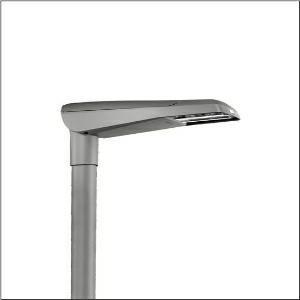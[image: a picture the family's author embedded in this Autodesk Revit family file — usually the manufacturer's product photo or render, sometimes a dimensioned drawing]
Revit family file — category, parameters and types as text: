
# Revit family: streetlight_sl_11_iq_micro___st1_2a_5xc1a61f08ce_98e9
name_source: partatom
category: Lighting Fixtures
units: mm (PartAtom-declared; Revit-internal decimal feet)

## family parameters
Cut with Voids When Loaded = No
Host = Face
Light Source = No
Part Type = Normal
Room Calculation Point = No
Round Connector Dimension = Use Diameter
Shared = No

## types (1)
- --- (1 x LED, 1690 lm, 12.6 W, 2700K)
    Apparent Load = 13 VA
    CIE Flux Codes = 33 71 96 100 100
    Color Rendering = 70
    Color Temperature = 2700K
    Default Elevation = 1800 mm
    Description = Streetlight SL 11 iQ micro, mast luminaire, primary light control with 3 zone facetted reflector, of plastic, silver coated, highly specular, primary optical cover: cover, of PMMA, transparent, light distribution: ST1.2a, light emission: direct distribution, primary light characteristic: asymmetric, installation type: side-entry, post-top, lamps: LED, High Power LED, rated values: 1.690lm | 12,6W | 134,1lm/W (begin service life); end service life: 1.690lm | 12,9W; at 50% lumin. flux: 845lm | 6,8W | 124,3lm/W, colour temperature: 2700K, colour rendering: CRI > 70, light colour: 727, light setting 1 begin service life: 100% | 1.690lm | 12,6W | 134,1lm/W | 2.700K, light setting 1 end service life: 12,9W, further light settings possible, control: optimised constant luminous flux control (CLO 2.0), Desk-Remote (wireless, voltage-free reading and setting of iQ features in the workshop via application-optimized NFC function/RFID function), Light-Fading, Smart-Wire, Night-Set, Lumen-Switch, Temp-Guard, Auto-Match, Street-Remote, with cable H07RN-F 3x 1.5mm², mains connection: 230..240V, AC, 50/60Hz, connection cable pre-assembled, cable length: 5,5m, luminaire housing, of diecast aluminium, powder-coated, SITECO metallic grey (DB 702S), please order mast flange separately, inclination adjustable without tools: 0°, 5°, 10°, 15° (post-top) | 0°, -5°, -10°, -15° (side-entry), sealing non-destructively replaceable, multi-level sealing system, length: 600mm, width: 174mm, height: 116mm, mast flange for spigot size: 42mm (side-entry): 5XC10008XM4, 60/48mm (side-entry/post-top): 5XC10108XM2, 76/60mm (side-entry/post-top): 5XC10108XM1, equipment: standard, protection rating (complete): IP66, insulation class (complete): insulation class II (safety insulation), certification: CE, ENEC, ENEC+, VDE, impact resistance: IK10, permissible operating ambient temperature for outdoor applications: -25..+50°C, standard-compliant lighting for roads and squares, Environmental Product Declaration (EPD) tested and certified by an independent institute, packaging unit: 1 piece

Light Distribution: ST1.2a
    Height = 116 mm
    Lamp = 1 x LED
    Lamp Light Flux = 1690 lm
    Lamp Power = 12.6 W
    Lamp count = 1
    Length = 600 mm
    Luminous efficacy = 134 lm/W
    Manufacturer = Siteco
    ModVariant = No
    Model = 5XC1A61F08CE
    Number of Poles = 1
    OnlyDefault = Yes
    Power Factor = 1
    Product Name = Streetlight SL 11 iQ micro | ST1.2a
    Product group = mast luminaire | pylon top
    ProductGroupID = 6100
    Protection Class = Protection class II
    Protection Degree = IP 66
    RLX_Detail_Level = 1
    RLX_Emergency_Light_Flux = 0 lm
    RLX_Emergency_Type = 0
    RLX_Emergency_Type_DB = No
    RlxData = <blob elided: 26545 chars, md5=fd692acd>
    Socket = socket
    Standby Power = 0 W
    System Light Flux = 1690 lm
    System Power = 13 W
    Type Comments = factory setting: luminous flux: 100 % | dim-lin: 254 | 229 mA
    Type Image = l_1006566.jpg
    URL = http://relux.com
    VarID = @adj_019005
    Voltage = 0 V
    Weight = 0.00 kg
    Width = 174 mm

## geometry (parser evidence)
native form markers: Blend x4, Sweep x9
no freeform markers — native parametric forms only
